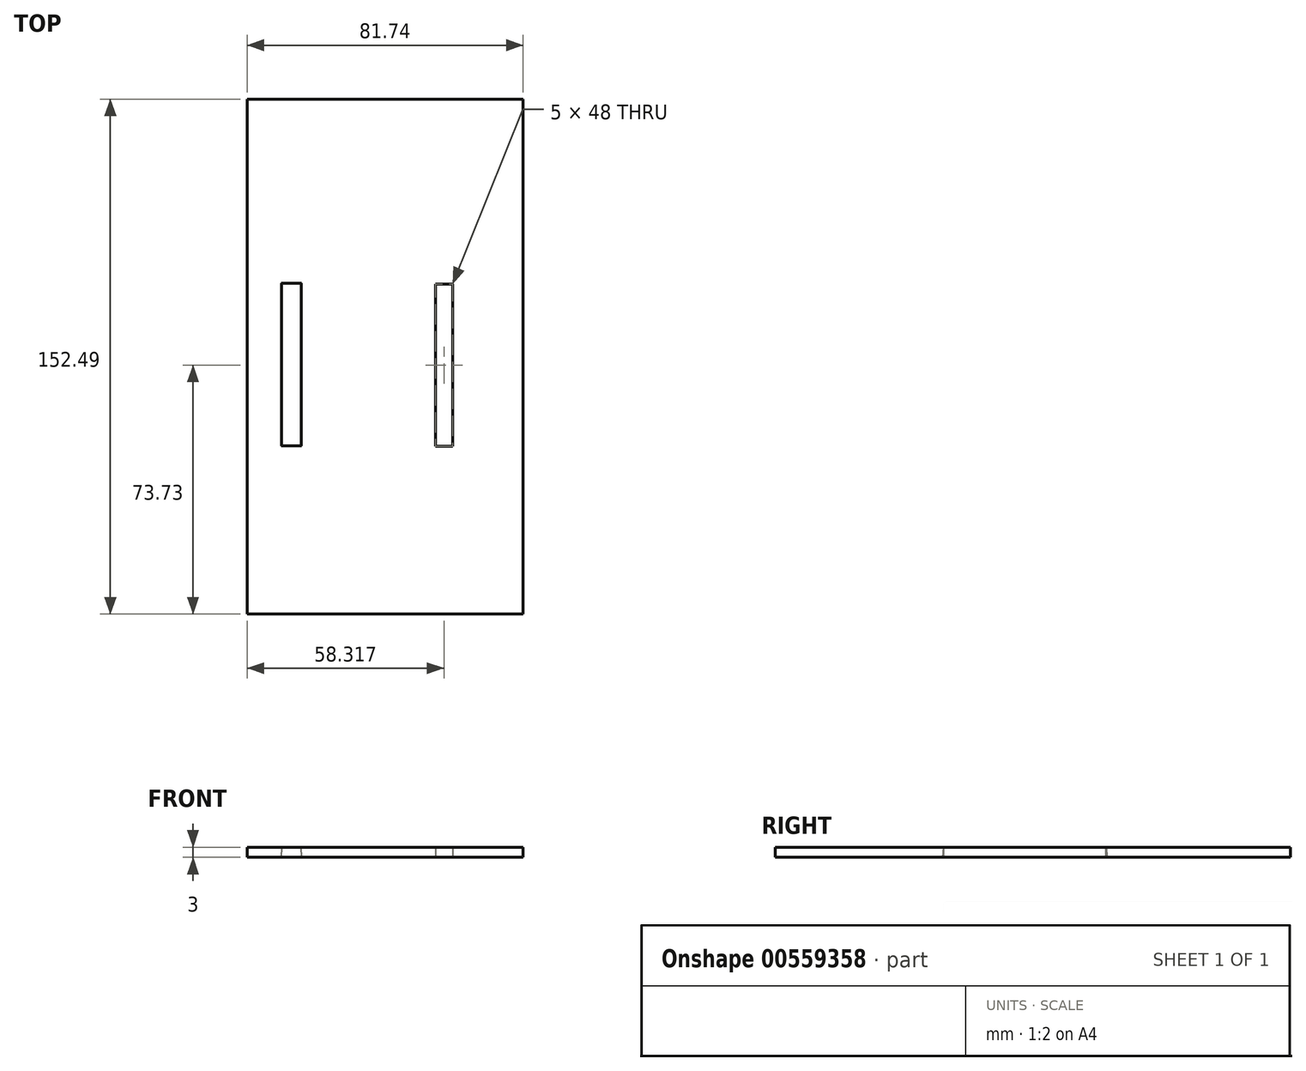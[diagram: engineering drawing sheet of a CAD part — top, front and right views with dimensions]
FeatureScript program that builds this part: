
annotation { "Feature Type Name" : "Feature", "Feature Type Description" : "" }
export const myFeature = defineFeature(function(context is Context, id is Id, definition is map)
    precondition{}
    {
        {
            var Q0;
            Q0=qCreatedBy(makeId("Top.planeOp"),FACE);
            var sketch = newSketch(context, id + "F0", { "sketchPlane" : qUnion([Q0])});
            skLineSegment(sketch, "E0.bottom", {"start": v(-50, 70) * mm, "end": v(50, 70) * mm});
            skLineSegment(sketch, "E0.top", {"start": v(-50, -70) * mm, "end": v(50, -70) * mm});
            skLineSegment(sketch, "E0.left", {"start": v(-50, 70) * mm, "end": v(-50, -70) * mm, "construction": true});
            skLineSegment(sketch, "E0.right", {"start": v(50, 70) * mm, "end": v(50, -70) * mm});
            skPoint(sketch, "E0.middle", {"position": v(0, 0) * mm});
            skLineSegment(sketch, "E1.bottom", {"start": v(-50, -33.68) * mm, "end": v(-50, -33.68) * mm});
            skLineSegment(sketch, "E1.top", {"start": v(-50, -39.68) * mm, "end": v(-50, -39.68) * mm});
            skLineSegment(sketch, "E1.left", {"start": v(-50, -33.68) * mm, "end": v(-50, -39.68) * mm});
            skLineSegment(sketch, "E1.right", {"start": v(-50, -33.68) * mm, "end": v(-50, -39.68) * mm});
            skLineSegment(sketch, "E2.bottom", {"start": v(-41.01, -39.68) * mm, "end": v(-36.01, -39.68) * mm});
            skLineSegment(sketch, "E2.top", {"start": v(-41.01, 8.32) * mm, "end": v(-36.01, 8.32) * mm});
            skLineSegment(sketch, "E2.left", {"start": v(-41.01, -39.68) * mm, "end": v(-41.01, 8.32) * mm});
            skLineSegment(sketch, "E2.right", {"start": v(-36.01, -39.68) * mm, "end": v(-36.01, 8.32) * mm});
            skSolve(sketch);
        }
        {
            var Q0;
            Q0 = qSketchRegion(id + "F0", true);
            var sketch = newSketch(context, id + "F1", { "sketchPlane" : qUnion([Q0])});
            skLineSegment(sketch, "E3.bottom", {"start": v(-15.1, -89.4) * mm, "end": v(-96.83, -89.4) * mm});
            skLineSegment(sketch, "E3.top", {"start": v(-15.1, 63.08) * mm, "end": v(-96.83, 63.08) * mm});
            skLineSegment(sketch, "E3.left", {"start": v(-15.1, -89.4) * mm, "end": v(-15.1, 63.08) * mm});
            skLineSegment(sketch, "E3.right", {"start": v(-96.83, -89.4) * mm, "end": v(-96.83, 63.08) * mm});
            skSolve(sketch);
        }
        {
            var Q0;
            Q0=makeQuery(id+"F1.imprint","IMPRINT",FACE,{"disambiguationData":[TD([[makeQuery(id+"F1.imprint","IMPRINT",EDGE,{"derivedFrom":sQuery(id+"F1.wireOp",EDGE,"E3.bottom")}),-1.0]])]});
            extrude(context, id + "F2", {"entities" : qUnion([Q0]), "depth" : 3 * mm, "offsetDistance" : 25 * mm});
        }
        {
            var Q0;
            Q0=makeQuery(id+"F2.opExtrude","CAP_FACE",FACE,{"disambiguationData":[OSD([sQuery(id+"F0.wireOp",EDGE,"E2.bottom"),sQuery(id+"F0.wireOp",EDGE,"E2.top"),sQuery(id+"F0.wireOp",EDGE,"E2.left"),sQuery(id+"F0.wireOp",EDGE,"E2.right"),sQuery(id+"F1.wireOp",EDGE,"E3.bottom"),sQuery(id+"F1.wireOp",EDGE,"E3.top"),sQuery(id+"F1.wireOp",EDGE,"E3.left"),sQuery(id+"F1.wireOp",EDGE,"E3.right")])],"isStart":false});
            var sketch = newSketch(context, id + "F3", { "sketchPlane" : qUnion([Q0])});
            skLineSegment(sketch, "E4.bottom", {"start": v(-86.63, 8.6) * mm, "end": v(-80.83, 8.6) * mm});
            skLineSegment(sketch, "E4.top", {"start": v(-86.63, -39.58) * mm, "end": v(-80.83, -39.58) * mm});
            skLineSegment(sketch, "E4.left", {"start": v(-86.63, 8.6) * mm, "end": v(-86.63, -39.58) * mm});
            skLineSegment(sketch, "E4.right", {"start": v(-80.83, 8.6) * mm, "end": v(-80.83, -39.58) * mm});
            skSolve(sketch);
        }
        {
            var Q0;
            Q0=makeQuery(id+"F3.imprint","IMPRINT",FACE,{"disambiguationData":[TD([[makeQuery(id+"F3.imprint","IMPRINT",EDGE,{"derivedFrom":sQuery(id+"F3.wireOp",EDGE,"E4.bottom")}),-1.0]])]});
            extrude(context, id + "F4", {"entities" : qUnion([Q0]), "operationType" : NewBodyOperationType.REMOVE, "oppositeDirection" : true, "depth" : 3 * mm, "offsetDistance" : 25 * mm, "hasDraft" : true, "draftAngle" : 3 * degree});
        }
    });
